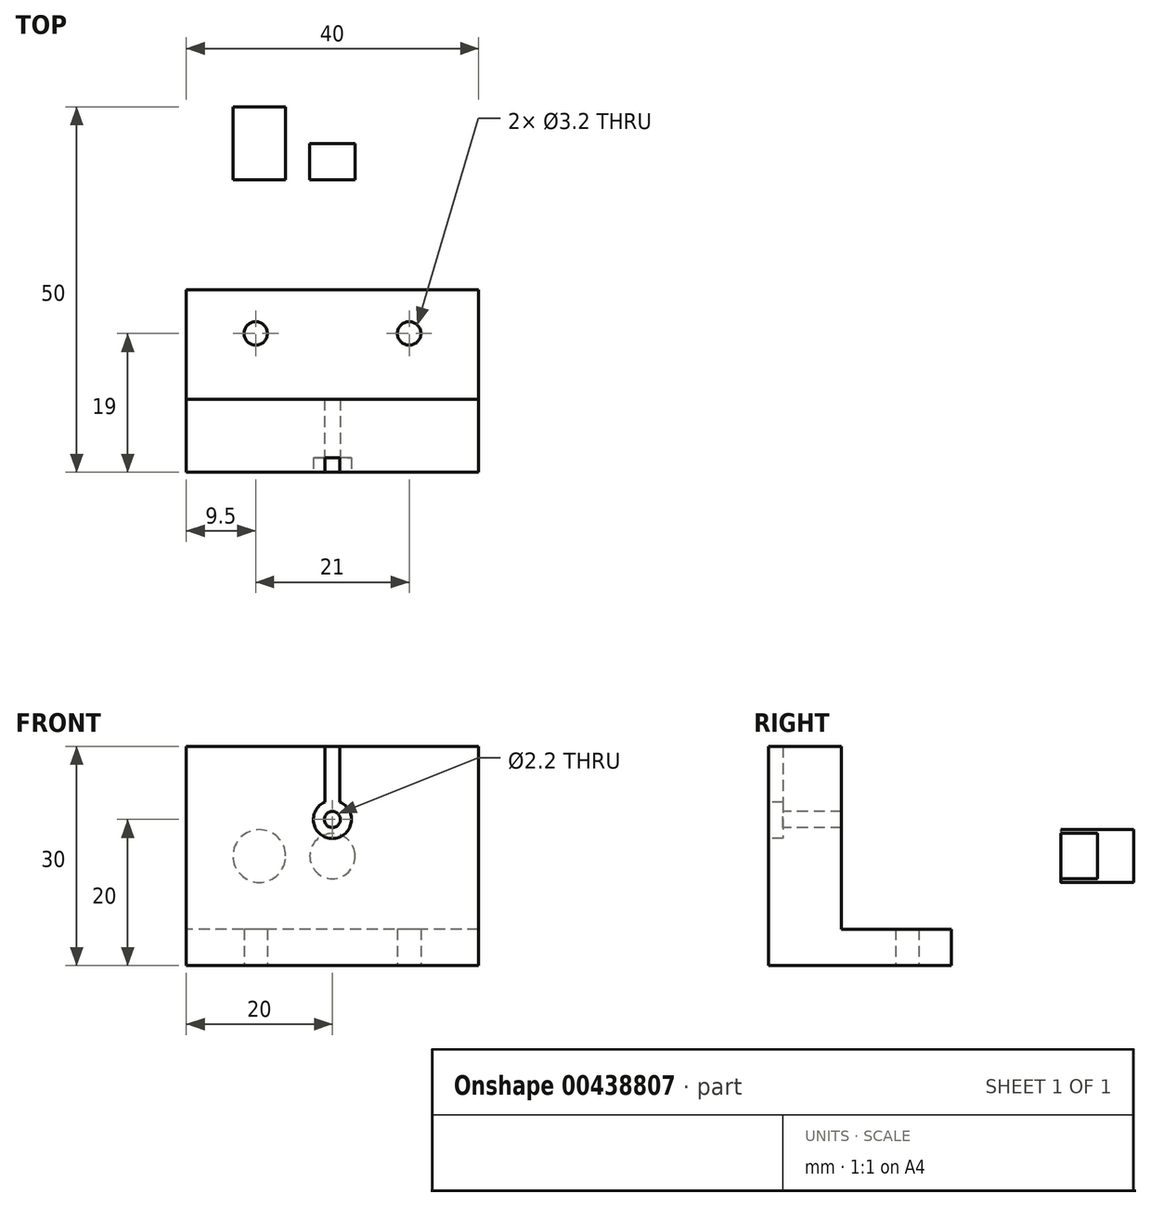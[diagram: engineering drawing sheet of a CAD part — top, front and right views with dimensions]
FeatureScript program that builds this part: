
annotation { "Feature Type Name" : "Feature", "Feature Type Description" : "" }
export const myFeature = defineFeature(function(context is Context, id is Id, definition is map)
    precondition{}
    {
        {
            var Q0;
            Q0=qCreatedBy(makeId("Right.planeOp"),FACE);
            var sketch = newSketch(context, id + "F0", { "sketchPlane" : qUnion([Q0])});
            skLineSegment(sketch, "E0.bottom", {"start": v(25, -15) * mm, "end": v(-25, -15) * mm});
            skLineSegment(sketch, "E0.top", {"start": v(25, 15) * mm, "end": v(15, 15) * mm});
            skLineSegment(sketch, "E0.left", {"start": v(25, -15) * mm, "end": v(25, 15) * mm});
            skLineSegment(sketch, "E0.right", {"start": v(-25, -15) * mm, "end": v(-25, 15) * mm});
            skPoint(sketch, "E0.middle", {"position": v(0, 0) * mm});
            skLineSegment(sketch, "E1", {"start": v(-15, 15) * mm, "end": v(-15, -10) * mm});
            skLineSegment(sketch, "E2", {"start": v(-15, -10) * mm, "end": v(15, -10) * mm});
            skLineSegment(sketch, "E3.MirrorCS", {"start": v(15, 15) * mm, "end": v(15, -10) * mm});
            skLineSegment(sketch, "E4.trimOffspring", {"start": v(-15, 15) * mm, "end": v(-25, 15) * mm});
            skSolve(sketch);
        }
        {
            var Q0;
            Q0 = qSketchRegion(id + "F0", true);
            extrude(context, id + "F1", {"entities" : qUnion([Q0]), "depth" : 40 * mm, "offsetDistance" : 25 * mm, "symmetric" : true});
        }
        {
            var Q0;
            Q0=makeQuery(id+"F1.opExtrude","SWEPT_FACE",FACE,{"disambiguationData":[OSD([sQuery(id+"F0.wireOp",EDGE,"E0.bottom")])]});
            var sketch = newSketch(context, id + "F2", { "sketchPlane" : qUnion([Q0])});
            skCircle(sketch, "E5", {"center": v(10.5, 6) * mm, "radius": 1.6 * mm});
            skCircle(sketch, "E6.MirrorC", {"center": v(10.5, -6) * mm, "radius": 1.6 * mm});
            skCircle(sketch, "E7.MirrorC", {"center": v(-10.5, 6) * mm, "radius": 1.6 * mm});
            skCircle(sketch, "E8.MirrorC", {"center": v(-10.5, -6) * mm, "radius": 1.6 * mm});
            skSolve(sketch);
        }
        {
            var Q0;
            Q0 = qSketchRegion(id + "F2", true);
            extrude(context, id + "F3", {"entities" : qUnion([Q0]), "operationType" : NewBodyOperationType.REMOVE, "oppositeDirection" : true, "depth" : 25 * mm, "offsetDistance" : 25 * mm});
        }
        {
            var Q0;
            Q0=makeQuery(id+"F1.opExtrude","SWEPT_FACE",FACE,{"disambiguationData":[OSD([sQuery(id+"F0.wireOp",EDGE,"E0.right")])]});
            var sketch = newSketch(context, id + "F4", { "sketchPlane" : qUnion([Q0])});
            skCircle(sketch, "E9", {"center": v(0, 5) * mm, "radius": 1.1 * mm});
            skArc(sketch, "E10", {"start": v(-1, 7.4) * mm, "mid": v(0, 2.4) * mm, "end": v(1, 7.4) * mm});
            skLineSegment(sketch, "E11", {"start": v(-1, 15) * mm, "end": v(-1, 7.4) * mm});
            skLineSegment(sketch, "E12.MirrorCS", {"start": v(1, 15) * mm, "end": v(1, 7.4) * mm});
            skSolve(sketch);
        }
        {
            var Q0;
            Q0=makeQuery(id+"F4.imprint","IMPRINT",FACE,{"disambiguationData":[TD([[makeQuery(id+"F4.imprint","IMPRINT",EDGE,{"derivedFrom":sQuery(id+"F4.wireOp",EDGE,"E9")}),1.0]])]});
            extrude(context, id + "F5", {"entities" : qUnion([Q0]), "operationType" : NewBodyOperationType.REMOVE, "oppositeDirection" : true, "depth" : 25 * mm, "offsetDistance" : 25 * mm});
        }
        {
            var Q0;
            Q0=makeQuery(id+"F4.imprint","IMPRINT",FACE,{"disambiguationData":[TD([[makeQuery(id+"F4.imprint","IMPRINT",EDGE,{"derivedFrom":sQuery(id+"F4.wireOp",EDGE,"E9")}),-1.0]])]});
            extrude(context, id + "F6", {"entities" : qUnion([Q0]), "operationType" : NewBodyOperationType.REMOVE, "oppositeDirection" : true, "depth" : 2 * mm, "offsetDistance" : 25 * mm});
        }
        {
            var Q0;
            Q0=makeQuery(id+"F1.opExtrude","SWEPT_FACE",FACE,{"disambiguationData":[OSD([sQuery(id+"F0.wireOp",EDGE,"E0.left")])]});
            var sketch = newSketch(context, id + "F7", { "sketchPlane" : qUnion([Q0])});
            skCircle(sketch, "E13", {"center": v(-10, 0) * mm, "radius": 3.6 * mm});
            skCircle(sketch, "E14.MirrorC", {"center": v(10, 0) * mm, "radius": 3.6 * mm});
            skCircle(sketch, "E15", {"center": v(0, 0) * mm, "radius": 3.1 * mm});
            skSolve(sketch);
        }
        {
            var Q0;
            Q0=makeQuery(id+"F7.imprint","IMPRINT",FACE,{"disambiguationData":[TD([[makeQuery(id+"F7.imprint","IMPRINT",EDGE,{"derivedFrom":sQuery(id+"F7.wireOp",EDGE,"E13")}),1.0]])]});
            var Q1;
            Q1=makeQuery(id+"F7.imprint","IMPRINT",FACE,{"disambiguationData":[TD([[makeQuery(id+"F7.imprint","IMPRINT",EDGE,{"derivedFrom":sQuery(id+"F7.wireOp",EDGE,"E14.MirrorC")}),-1.0]])]});
            extrude(context, id + "F8", {"entities" : qUnion([Q0, Q1]), "operationType" : NewBodyOperationType.REMOVE, "oppositeDirection" : true, "depth" : 25 * mm, "offsetDistance" : 25 * mm});
        }
        {
            var Q0;
            Q0=makeQuery(id+"F7.imprint","IMPRINT",FACE,{"disambiguationData":[TD([[makeQuery(id+"F7.imprint","IMPRINT",EDGE,{"derivedFrom":sQuery(id+"F7.wireOp",EDGE,"E15")}),1.0]])]});
            extrude(context, id + "F9", {"entities" : qUnion([Q0]), "operationType" : NewBodyOperationType.REMOVE, "oppositeDirection" : true, "depth" : 5 * mm, "offsetDistance" : 25 * mm});
        }
    });
